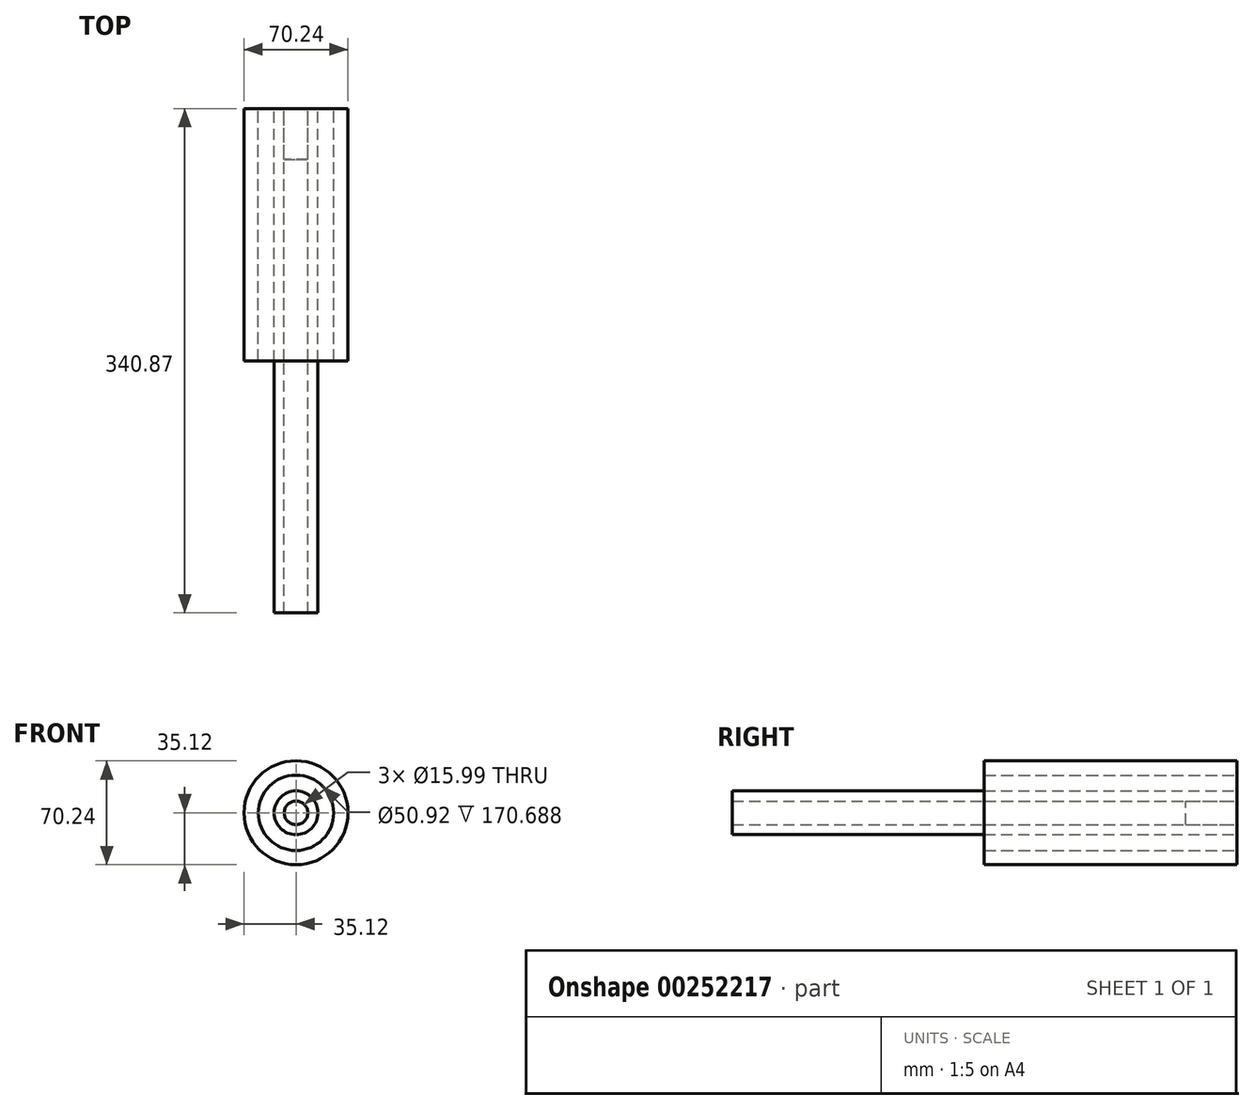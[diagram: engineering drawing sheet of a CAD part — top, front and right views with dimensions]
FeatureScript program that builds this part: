
annotation { "Feature Type Name" : "Feature", "Feature Type Description" : "" }
export const myFeature = defineFeature(function(context is Context, id is Id, definition is map)
    precondition{}
    {
        {
            var Q0;
            Q0=qCreatedBy(makeId("Front.planeOp"),FACE);
            var sketch = newSketch(context, id + "F0", { "sketchPlane" : qUnion([Q0])});
            skCircle(sketch, "E0", {"center": v(0, 0) * mm, "radius": 35.12 * mm});
            skCircle(sketch, "E1", {"center": v(0, 0) * mm, "radius": 25.46 * mm});
            skSolve(sketch);
        }
        {
            var Q0;
            Q0=makeQuery(id+"F0.imprint","IMPRINT",FACE,{"disambiguationData":[TD([[makeQuery(id+"F0.imprint","IMPRINT",EDGE,{"derivedFrom":sQuery(id+"F0.wireOp",EDGE,"E1")}),1.0]])]});
            var sketch = newSketch(context, id + "F1", { "sketchPlane" : qUnion([Q0])});
            skCircle(sketch, "E2", {"center": v(0, 0) * mm, "radius": 14.81 * mm});
            skCircle(sketch, "E3", {"center": v(0, 0) * mm, "radius": 8 * mm});
            skSolve(sketch);
        }
        {
            var Q0;
            Q0 = qSketchRegion(id + "F0", true);
            var Q1;
            Q1 = qSketchRegion(id + "F1", true);
            extrude(context, id + "F2", {"entities" : qUnion([Q0, Q1]), "depth" : 170.7 * mm});
        }
        {
            var Q0;
            Q0=makeQuery(id+"F1.imprint","IMPRINT",FACE,{"disambiguationData":[TD([[makeQuery(id+"F1.imprint","IMPRINT",EDGE,{"derivedFrom":sQuery(id+"F1.wireOp",EDGE,"E2")}),1.0]])]});
            var Q1;
            Q1=makeQuery(id+"F1.imprint","IMPRINT",FACE,{"disambiguationData":[TD([[makeQuery(id+"F1.imprint","IMPRINT",EDGE,{"derivedFrom":sQuery(id+"F1.wireOp",EDGE,"E2")}),-1.0]])]});
            var Q2;
            Q2=makeQuery(id+"F2.opExtrude","CAP_FACE",FACE,{"disambiguationData":[OSD([sQuery(id+"F1.wireOp",EDGE,"E2"),sQuery(id+"F1.wireOp",EDGE,"E3")])],"isStart":false});
            extrude(context, id + "F3", {"entities" : qUnion([Q0, Q1, Q2]), "depth" : 170.18 * mm});
        }
        {
            var Q0;
            Q0=makeQuery(id+"F1.imprint","IMPRINT",FACE,{"disambiguationData":[TD([[makeQuery(id+"F1.imprint","IMPRINT",EDGE,{"derivedFrom":sQuery(id+"F1.wireOp",EDGE,"E3")}),1.0]])]});
            extrude(context, id + "F4", {"entities" : qUnion([Q0]), "depth" : 34.54 * mm});
        }
    });
